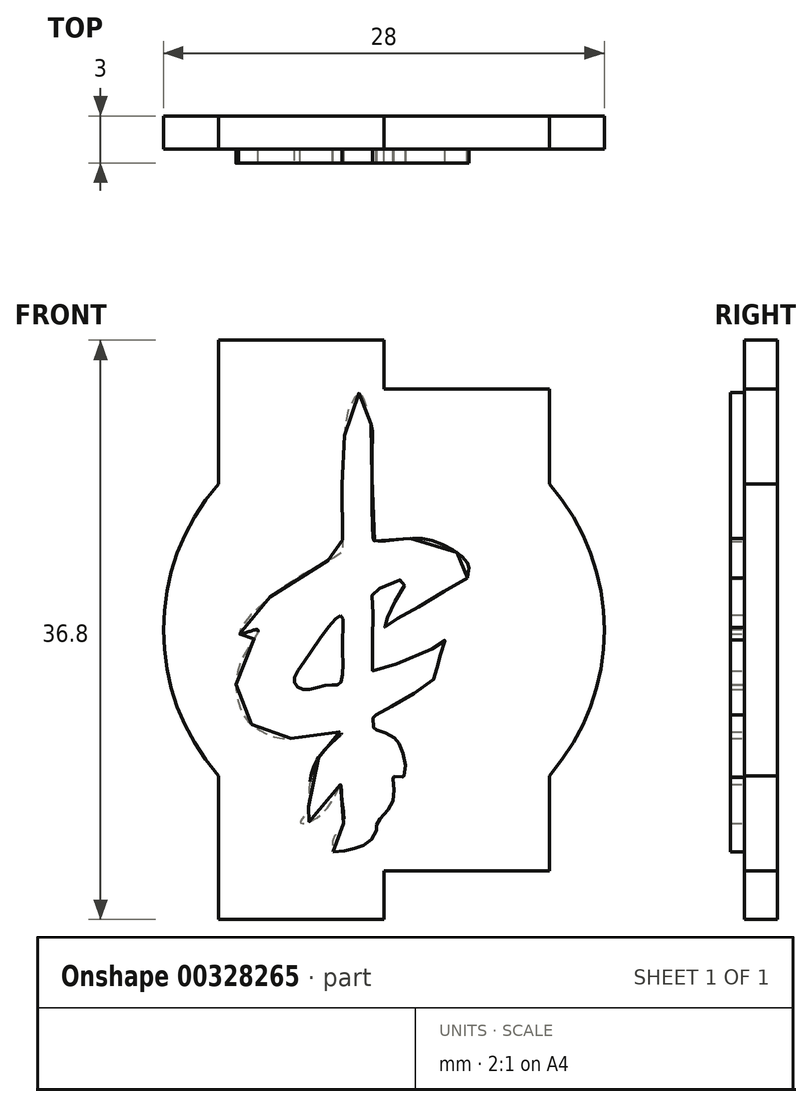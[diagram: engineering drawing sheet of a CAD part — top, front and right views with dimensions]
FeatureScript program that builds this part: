
annotation { "Feature Type Name" : "Feature", "Feature Type Description" : "" }
export const myFeature = defineFeature(function(context is Context, id is Id, definition is map)
    precondition{}
    {
        {
            var Q0;
            Q0=qCreatedBy(makeId("Front.planeOp"),FACE);
            var sketch = newSketch(context, id + "F0", { "sketchPlane" : qUnion([Q0])});
            skArc(sketch, "E0", {"start": v(-10.5, 9.26) * mm, "mid": v(-14, 0) * mm, "end": v(-10.5, -9.26) * mm});
            skLineSegment(sketch, "E1", {"start": v(0, 15.14) * mm, "end": v(10.5, 15.14) * mm});
            skLineSegment(sketch, "E2", {"start": v(0, -15.3) * mm, "end": v(10.5, -15.3) * mm});
            skLineSegment(sketch, "E3", {"start": v(0, -18.4) * mm, "end": v(-10.5, -18.4) * mm});
            skLineSegment(sketch, "E4", {"start": v(0, 18.4) * mm, "end": v(-10.5, 18.4) * mm});
            skLineSegment(sketch, "E5", {"start": v(10.5, 15.14) * mm, "end": v(10.5, 9.26) * mm});
            skLineSegment(sketch, "E6", {"start": v(-10.5, 18.4) * mm, "end": v(-10.5, 9.26) * mm});
            skLineSegment(sketch, "E7", {"start": v(0, 18.4) * mm, "end": v(0, 15.14) * mm});
            skLineSegment(sketch, "E8", {"start": v(0, -15.3) * mm, "end": v(0, -18.4) * mm});
            skLineSegment(sketch, "E9.trimOffspring", {"start": v(-10.5, -9.26) * mm, "end": v(-10.5, -18.4) * mm});
            skLineSegment(sketch, "E10.trimOffspring", {"start": v(10.5, -9.26) * mm, "end": v(10.5, -15.3) * mm});
            skArc(sketch, "E11.trimOffspring", {"start": v(10.5, -9.26) * mm, "mid": v(14, 0) * mm, "end": v(10.5, 9.26) * mm});
            skFitSpline(sketch, "E12", {"points": [v(-3.24, -14.11) * mm, v(-1.88, -13.87) * mm, v(-0.93, -13.44) * mm, v(-0.44, -12.56) * mm, v(-0.48, -12.35) * mm, v(0.26, -11.44) * mm, v(0.64, -10.27) * mm, v(0.56, -9.28) * mm, v(0.6, -9.3) * mm, v(1.24, -9.37) * mm, v(1.25, -9.38) * mm, v(1.36, -8.8) * mm, v(1, -7.28) * mm, v(0.58, -6.81) * mm, v(-0.47, -6.35) * mm, v(-0.65, -6.3) * mm, v(-0.7, -5.5) * mm, v(-0.51, -5.4) * mm], "startDerivative": vector(17.79, -0.05) * mm, "endDerivative": vector(22.24, 7.82) * mm});
            skFitSpline(sketch, "E13", {"points": [v(-0.51, -5.4) * mm, v(0.96, -4.59) * mm, v(3.25, -3.03) * mm, v(3.38, -2.47) * mm, v(3.55, -1.67) * mm, v(3.87, -0.66) * mm, v(3.45, -0.97) * mm, v(-0.7, -2.6) * mm, v(-0.73, -2.46) * mm, v(-0.74, -1.48) * mm, v(-0.68, 1.23) * mm, v(-0.7, 2.37) * mm, v(-0.23, 2.66) * mm, v(1.38, 3.21) * mm, v(0.98, 2.3) * mm, v(0.37, 1.1) * mm, v(0, 0.17) * mm, v(0.33, 0.39) * mm, v(2.19, 1.47) * mm, v(5.3, 3.31) * mm], "startDerivative": vector(17.66, 9.23) * mm, "endDerivative": vector(28.66, 15.06) * mm});
            skFitSpline(sketch, "E14", {"points": [v(5.3, 3.31) * mm, v(5.3, 3.3) * mm, v(5.36, 3.68) * mm, v(5.33, 4.24) * mm, v(3.56, 5.5) * mm, v(1.57, 5.8) * mm, v(0, 5.64) * mm, v(-0.63, 5.67) * mm, v(-0.7, 5.78) * mm, v(-0.74, 11.56) * mm, v(-0.78, 12.94) * mm, v(-1.26, 14.63) * mm, v(-1.5, 15.07) * mm, v(-2.22, 14.07) * mm, v(-2.53, 11.7) * mm, v(-2.64, 9.52) * mm, v(-2.65, 6.3) * mm, v(-2.62, 5.16) * mm, v(-2.68, 4.9) * mm, v(-4.04, 4.15) * mm, v(-7.99, 1.42) * mm, v(-9.22, -0.23) * mm, v(-8.74, -0.17) * mm, v(-8, 0) * mm, v(-8.73, -1.32) * mm, v(-9.4, -3.38) * mm, v(-8.95, -5.35) * mm, v(-7.87, -6.4) * mm, v(-6.3, -6.89) * mm, v(-3.54, -6.56) * mm, v(-2.7, -6.51) * mm, v(-2.83, -6.73) * mm, v(-4.34, -8.42) * mm, v(-4.78, -11) * mm, v(-4.95, -11.7) * mm, v(-5.32, -12.25) * mm, v(-3.87, -11.62) * mm, v(-2.75, -9.83) * mm, v(-2.7, -10.5) * mm, v(-2.62, -12.43) * mm, v(-3.19, -13.2) * mm, v(-3.24, -14.11) * mm], "startDerivative": vector(18.59, 5.41) * mm, "endDerivative": vector(-0.77, -37.03) * mm});
            skFitSpline(sketch, "E15", {"points": [v(-2.75, 0.9) * mm, v(-4.99, -1.9) * mm, v(-5.7, -3.34) * mm, v(-5.06, -3.8) * mm, v(-3.6, -3.5) * mm, v(-2.79, -3.41) * mm, v(-2.63, -0.94) * mm, v(-2.75, 0.9) * mm]});
            skSolve(sketch);
        }
        {
            var Q0;
            {var subQ0=sQuery(id+"F0.wireOp",EDGE,"E12");Q0=makeQuery(id+"F0.imprint","IMPRINT",FACE,{"disambiguationData":[TD([[makeQuery(id+"F0.imprint","IMPRINT",EDGE,{"derivedFrom":subQ0}),1.0]])]});}
            extrude(context, id + "F1", {"entities" : qUnion([Q0]), "flatOperationType" : FlatOperationType.REMOVE, "offsetDistance" : 25 * mm, "depth" : 3 * mm, "domain" : OperationDomain.MODEL});
        }
        {
            var Q0;
            Q0=qCreatedBy(makeId("Front.planeOp"),FACE);
            var sketch = newSketch(context, id + "F2", { "sketchPlane" : qUnion([Q0])});
            skLineSegment(sketch, "E16", {"start": v(0, 15.3) * mm, "end": v(10.5, 15.3) * mm});
            skLineSegment(sketch, "E17", {"start": v(10.5, 15.3) * mm, "end": v(10.5, 9.18) * mm});
            skLineSegment(sketch, "E18", {"start": v(10.5, -9.26) * mm, "end": v(10.5, -15.3) * mm});
            skLineSegment(sketch, "E19", {"start": v(10.5, -15.3) * mm, "end": v(0, -15.3) * mm});
            skLineSegment(sketch, "E20", {"start": v(0, -15.3) * mm, "end": v(0, -18.4) * mm});
            skLineSegment(sketch, "E21", {"start": v(0, -18.4) * mm, "end": v(-10.5, -18.4) * mm});
            skLineSegment(sketch, "E22", {"start": v(-10.5, -18.4) * mm, "end": v(-10.5, -9.26) * mm});
            skLineSegment(sketch, "E23", {"start": v(-10.5, 18.4) * mm, "end": v(0, 18.4) * mm});
            skLineSegment(sketch, "E24", {"start": v(0, 18.4) * mm, "end": v(0, 15.3) * mm});
            skArc(sketch, "E25", {"start": v(-10.5, 9.26) * mm, "mid": v(-14, 0) * mm, "end": v(-10.5, -9.26) * mm});
            skLineSegment(sketch, "E26.trimOffspring", {"start": v(-10.5, 9.26) * mm, "end": v(-10.5, 18.4) * mm});
            skArc(sketch, "E27.trimOffspring", {"start": v(10.5, -9.26) * mm, "mid": v(14, 0) * mm, "end": v(10.5, 9.26) * mm});
            skSolve(sketch);
        }
        {
            var Q0;
            Q0 = qSketchRegion(id + "F2", true);
            extrude(context, id + "F3", {"entities" : qUnion([Q0]), "operationType" : NewBodyOperationType.ADD, "depth" : 2.1 * mm});
        }
    });
